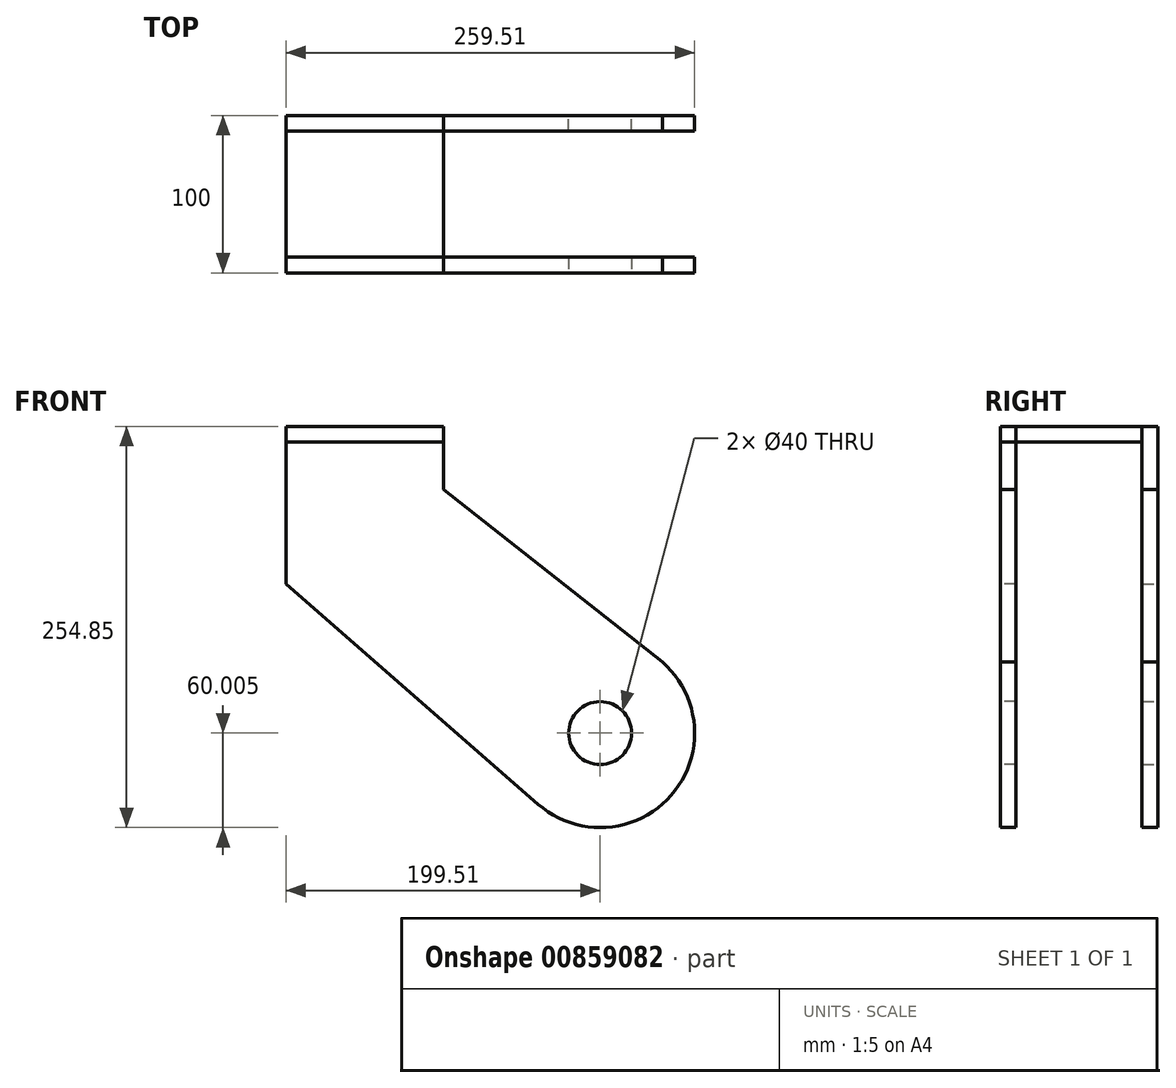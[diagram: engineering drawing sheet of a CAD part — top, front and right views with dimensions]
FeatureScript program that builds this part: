
annotation { "Feature Type Name" : "Feature", "Feature Type Description" : "" }
export const myFeature = defineFeature(function(context is Context, id is Id, definition is map)
    precondition{}
    {
        {
            var Q0;
            Q0=qCreatedBy(makeId("Front.planeOp"),FACE);
            var sketch = newSketch(context, id + "F0", { "sketchPlane" : qUnion([Q0])});
            skLineSegment(sketch, "E0", {"start": v(0, 0) * mm, "end": v(100, 0) * mm});
            skLineSegment(sketch, "E1", {"start": v(100, 0) * mm, "end": v(100, -40) * mm});
            skLineSegment(sketch, "E2", {"start": v(0, 0) * mm, "end": v(0, -100) * mm});
            skLineSegment(sketch, "E3", {"start": v(0, 0) * mm, "end": v(50, 0) * mm});
            skLineSegment(sketch, "E4", {"start": v(0, -100) * mm, "end": v(160, -240) * mm});
            skArc(sketch, "E5", {"start": v(160, -240) * mm, "mid": v(244.66, -234.36) * mm, "end": v(239.02, -149.7) * mm});
            skLineSegment(sketch, "E6", {"start": v(239.02, -149.7) * mm, "end": v(100, -40) * mm});
            skCircle(sketch, "E7", {"center": v(199.51, -194.85) * mm, "radius": 20 * mm});
            skSolve(sketch);
        }
        {
            var Q0;
            Q0=makeQuery(id+"F0.imprint","IMPRINT",FACE,{"disambiguationData":[TD([[makeQuery(id+"F0.imprint","IMPRINT",EDGE,{"derivedFrom":sQuery(id+"F0.wireOp",EDGE,"E0")}),-1.0]])]});
            extrude(context, id + "F1", {"entities" : qUnion([Q0]), "depth" : 10 * mm, "offsetDistance" : 25 * mm});
        }
        {
            var Q0;
            Q0=makeQuery(id+"F1.opExtrude","CAP_FACE",FACE,{"disambiguationData":[OSD([sQuery(id+"F0.wireOp",EDGE,"E0"),sQuery(id+"F0.wireOp",EDGE,"E1"),sQuery(id+"F0.wireOp",EDGE,"E2"),sQuery(id+"F0.wireOp",EDGE,"E3"),sQuery(id+"F0.wireOp",EDGE,"E4"),sQuery(id+"F0.wireOp",EDGE,"E5"),sQuery(id+"F0.wireOp",EDGE,"E6"),sQuery(id+"F0.wireOp",EDGE,"E7")])],"isStart":false});
            cPlane(context, id + "F2", {"entities" : qUnion([Q0]), "cplaneType" : CPlaneType.OFFSET, "offset" : 40 * mm, "width" : 150 * mm, "height" : 150 * mm});
        }
        {
            var Q0;
            Q0=makeQuery(id+"F1.opExtrude","SWEPT_BODY",BODY,{"disambiguationData":[OSD([sQuery(id+"F0.wireOp",EDGE,"E0"),sQuery(id+"F0.wireOp",EDGE,"E1"),sQuery(id+"F0.wireOp",EDGE,"E2"),sQuery(id+"F0.wireOp",EDGE,"E3"),sQuery(id+"F0.wireOp",EDGE,"E4"),sQuery(id+"F0.wireOp",EDGE,"E5"),sQuery(id+"F0.wireOp",EDGE,"E6"),sQuery(id+"F0.wireOp",EDGE,"E7")])]});
            var Q1;
            Q1=qCreatedBy(id+"F2.planeOp",FACE);
            mirror(context, id + "F3", {"entities" : qUnion([Q0]), "mirrorPlane" : qUnion([Q1])});
        }
        {
            var Q0;
            Q0=makeQuery(id+"F1.opExtrude","CAP_FACE",FACE,{"disambiguationData":[OSD([sQuery(id+"F0.wireOp",EDGE,"E0"),sQuery(id+"F0.wireOp",EDGE,"E1"),sQuery(id+"F0.wireOp",EDGE,"E2"),sQuery(id+"F0.wireOp",EDGE,"E3"),sQuery(id+"F0.wireOp",EDGE,"E4"),sQuery(id+"F0.wireOp",EDGE,"E5"),sQuery(id+"F0.wireOp",EDGE,"E6"),sQuery(id+"F0.wireOp",EDGE,"E7")])],"isStart":false});
            var sketch = newSketch(context, id + "F4", { "sketchPlane" : qUnion([Q0])});
            skLineSegment(sketch, "E8", {"start": v(100, 0) * mm, "end": v(100, -10) * mm});
            skLineSegment(sketch, "E9", {"start": v(100, -10) * mm, "end": v(0, -10) * mm});
            skLineSegment(sketch, "E10", {"start": v(0, -10) * mm, "end": v(0, 0) * mm});
            skLineSegment(sketch, "E11", {"start": v(0, 0) * mm, "end": v(100, 0) * mm});
            skSolve(sketch);
        }
        {
            var Q0;
            Q0=makeQuery(id+"F4.imprint","IMPRINT",FACE,{"disambiguationData":[TD([[makeQuery(id+"F4.imprint","IMPRINT",EDGE,{"derivedFrom":sQuery(id+"F4.wireOp",EDGE,"E8")}),-1.0]])]});
            extrude(context, id + "F5", {"entities" : qUnion([Q0]), "depth" : 90 * mm, "offsetDistance" : 25 * mm});
        }
    });
